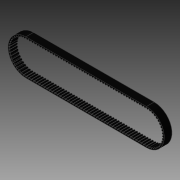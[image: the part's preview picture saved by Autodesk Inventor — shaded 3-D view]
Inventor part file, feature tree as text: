
AUTODESK INVENTOR PART (.ipt)
format: ipt  version: 2014 SP1 (Build 180222100, 222)  size: 1,265,152 bytes
history: native  units: in
note: dims shown in document units (in); Inventor stores cm internally (conversion verified against a paired STEP export)
features: extrude x2, sketch x1, pattern_linear x1
ambient origin geometry x8: Origin, YZ Plane, XZ Plane, XY Plane, X Axis, Y Axis, Z Axis, Center Point
bodies: Solid1 (feature_tree)
feature tree (4):
  sketch  "Sketch1"  dims[d0=1.29in d1=9.2008in d2=1.3315in d3=0.5906in d4=0.0in d6=52.7559in d8=0.0039in d9=0.0681in d10=0.5906in d11=0.0in]
  extrude  "Extrusion1"  Depth=9.2008in
  pattern_linear  "Rectangular Pattern1"  Spacing1=1.3315in  [1 undecoded]
  extrude  "Extrusion2"  Depth=0.5906in TaperAngle=0.0deg
note: 1 required parameter value undecoded (feature->parameter linkage not recoverable at this tier; creation-order binding heuristic only, values carry confidence <= 0.55)
